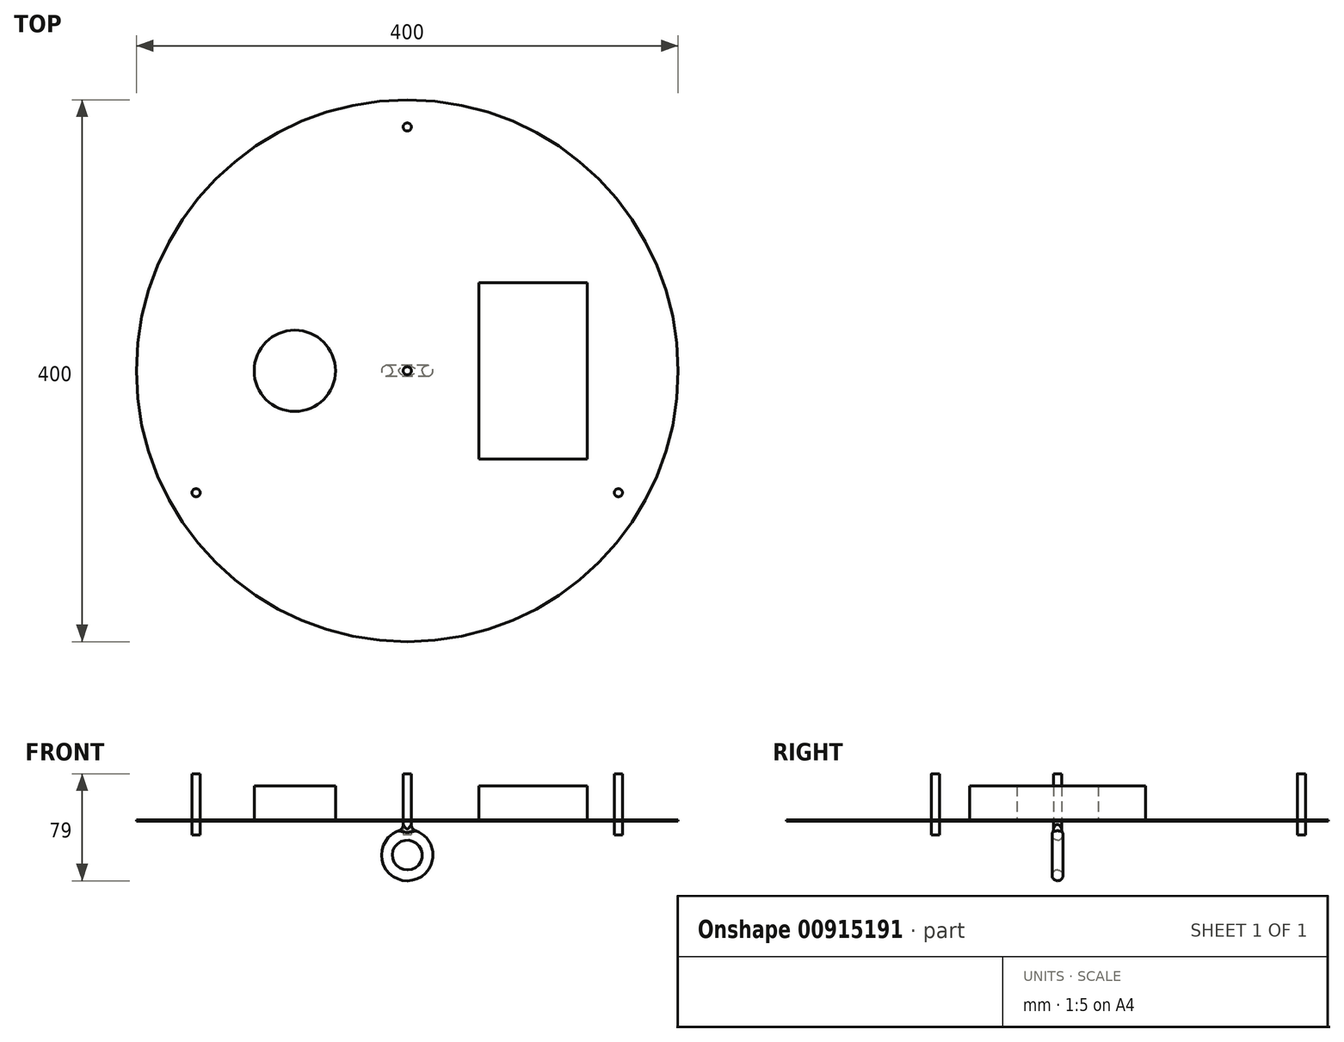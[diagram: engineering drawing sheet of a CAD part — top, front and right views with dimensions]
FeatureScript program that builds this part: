
annotation { "Feature Type Name" : "Feature", "Feature Type Description" : "" }
export const myFeature = defineFeature(function(context is Context, id is Id, definition is map)
    precondition{}
    {
        {
            var Q0;
            Q0=qCreatedBy(makeId("Top.planeOp"),FACE);
            var sketch = newSketch(context, id + "F0", { "sketchPlane" : qUnion([Q0])});
            skCircle(sketch, "E0", {"center": v(0, 0) * mm, "radius": 200 * mm});
            skCircle(sketch, "E1", {"center": v(0, 0) * mm, "radius": 3 * mm});
            skCircle(sketch, "E2", {"center": v(0, 180) * mm, "radius": 3 * mm});
            skCircle(sketch, "E3.1.0", {"center": v(-155.88, -90) * mm, "radius": 3 * mm});
            skCircle(sketch, "E3.2.0", {"center": v(155.88, -90) * mm, "radius": 3 * mm});
            skSolve(sketch);
        }
        {
            var Q0;
            Q0=makeQuery(id+"F0.imprint","IMPRINT",FACE,{"disambiguationData":[TD([[makeQuery(id+"F0.imprint","IMPRINT",EDGE,{"derivedFrom":sQuery(id+"F0.wireOp",EDGE,"E0")}),1.0]])]});
            extrude(context, id + "F1", {"entities" : qUnion([Q0]), "depth" : 1 * mm, "offsetDistance" : 25 * mm});
        }
        {
            var Q0;
            Q0=makeQuery(id+"F1.opExtrude","CAP_FACE",FACE,{"disambiguationData":[OSD([sQuery(id+"F0.wireOp",EDGE,"E0"),sQuery(id+"F0.wireOp",EDGE,"E1"),sQuery(id+"F0.wireOp",EDGE,"E2"),sQuery(id+"F0.wireOp",EDGE,"E3.1.0"),sQuery(id+"F0.wireOp",EDGE,"E3.2.0")])],"isStart":false});
            var sketch = newSketch(context, id + "F2", { "sketchPlane" : qUnion([Q0])});
            skCircle(sketch, "E4", {"center": v(-83, 0) * mm, "radius": 30 * mm});
            skLineSegment(sketch, "E5.bottom", {"start": v(133, -65) * mm, "end": v(53, -65) * mm});
            skLineSegment(sketch, "E5.top", {"start": v(133, 65) * mm, "end": v(53, 65) * mm});
            skLineSegment(sketch, "E5.left", {"start": v(133, -65) * mm, "end": v(133, 65) * mm});
            skLineSegment(sketch, "E5.right", {"start": v(53, -65) * mm, "end": v(53, 65) * mm});
            skPoint(sketch, "E5.middle", {"position": v(93, 0) * mm});
            skSolve(sketch);
        }
        {
            var Q0;
            Q0 = qSketchRegion(id + "F2", true);
            extrude(context, id + "F3", {"entities" : qUnion([Q0]), "operationType" : NewBodyOperationType.ADD, "depth" : 25 * mm, "offsetDistance" : 25 * mm});
        }
        {
            var Q0;
            Q0=makeQuery(id+"F0.imprint","IMPRINT",FACE,{"disambiguationData":[TD([[makeQuery(id+"F0.imprint","IMPRINT",EDGE,{"derivedFrom":sQuery(id+"F0.wireOp",EDGE,"E3.1.0")}),1.0]])]});
            var Q1;
            Q1=makeQuery(id+"F0.imprint","IMPRINT",FACE,{"disambiguationData":[TD([[makeQuery(id+"F0.imprint","IMPRINT",EDGE,{"derivedFrom":sQuery(id+"F0.wireOp",EDGE,"E1")}),1.0]])]});
            var Q2;
            Q2=makeQuery(id+"F0.imprint","IMPRINT",FACE,{"disambiguationData":[TD([[makeQuery(id+"F0.imprint","IMPRINT",EDGE,{"derivedFrom":sQuery(id+"F0.wireOp",EDGE,"E3.2.0")}),1.0]])]});
            var Q3;
            Q3=makeQuery(id+"F0.imprint","IMPRINT",FACE,{"disambiguationData":[TD([[makeQuery(id+"F0.imprint","IMPRINT",EDGE,{"derivedFrom":sQuery(id+"F0.wireOp",EDGE,"E2")}),1.0]])]});
            extrude(context, id + "F4", {"entities" : qUnion([Q0, Q1, Q2, Q3]), "operationType" : NewBodyOperationType.ADD, "depth" : 35 * mm, "offsetDistance" : 25 * mm, "hasSecondDirection" : true, "secondDirectionOppositeDirection" : true, "secondDirectionDepth" : 10 * mm});
        }
        {
            var Q0;
            Q0=qCreatedBy(makeId("Front.planeOp"),FACE);
            var sketch = newSketch(context, id + "F5", { "sketchPlane" : qUnion([Q0])});
            skLineSegment(sketch, "E6", {"start": v(0, -10) * mm, "end": v(0, -15) * mm});
            skCircle(sketch, "E7", {"center": v(0, -25) * mm, "radius": 10 * mm});
            skSolve(sketch);
        }
        {
            var Q0;
            Q0=qCreatedBy(makeId("Right.planeOp"),FACE);
            var sketch = newSketch(context, id + "F6", { "sketchPlane" : qUnion([Q0])});
            skCircle(sketch, "E8", {"center": v(0, -10) * mm, "radius": 4 * mm});
            skSolve(sketch);
        }
        {
            var Q0;
            Q0=makeQuery(id+"F6.imprint","IMPRINT",FACE,{"disambiguationData":[TD([[makeQuery(id+"F6.imprint","IMPRINT",EDGE,{"derivedFrom":sQuery(id+"F6.wireOp",EDGE,"E8")}),1.0]])]});
            var Q1;
            Q1=sQuery(id+"F6.wireOp",EDGE,"E8");
            var Q2;
            Q2=sQuery(id+"F5.wireOp",EDGE,"E7");
            sweep(context, id + "F7", {"operationType" : NewBodyOperationType.ADD, "profiles" : qUnion([Q0]), "surfaceProfiles" : qUnion([Q1]), "path" : qUnion([Q2])});
        }
        {
            var Q0;
            {var subQ0=sQuery(id+"F0.wireOp",EDGE,"E1");Q0=makeQuery(id+"F7.boolean.opBoolean","INTERSECT",EDGE,{"disambiguationData":[OD(0.0)],"derivedFrom":[makeQuery(id+"F4.boolean.opBoolean","SPLIT",FACE,{"disambiguationData":[TD([makeQuery(id+"F4.opExtrude","CAP_FACE",FACE,{"disambiguationData":[OSD([subQ0])],"isStart":true})])],"derivedFrom":makeQuery(id+"F4.opExtrude","SWEPT_FACE",FACE,{"disambiguationData":[OSD([subQ0])]})}),makeQuery(id+"F7.opSweep","SWEPT_FACE",FACE,{"disambiguationData":[OSD([sQuery(id+"F5.wireOp",EDGE,"E7"),sQuery(id+"F6.wireOp",EDGE,"E8")])]})]});}
            var Q1;
            {var subQ0=sQuery(id+"F0.wireOp",EDGE,"E1");Q1=makeQuery(id+"F7.boolean.opBoolean","INTERSECT",EDGE,{"disambiguationData":[OD(1.0)],"derivedFrom":[makeQuery(id+"F4.boolean.opBoolean","SPLIT",FACE,{"disambiguationData":[TD([makeQuery(id+"F4.opExtrude","CAP_FACE",FACE,{"disambiguationData":[OSD([subQ0])],"isStart":true})])],"derivedFrom":makeQuery(id+"F4.opExtrude","SWEPT_FACE",FACE,{"disambiguationData":[OSD([subQ0])]})}),makeQuery(id+"F7.opSweep","SWEPT_FACE",FACE,{"disambiguationData":[OSD([sQuery(id+"F5.wireOp",EDGE,"E7"),sQuery(id+"F6.wireOp",EDGE,"E8")])]})]});}
            fillet(context, id + "F8", {"entities" : qUnion([Q0, Q1]), "radius" : 5 * mm, "tangentPropagation" : true, "allowEdgeOverflow" : false});
        }
    });
